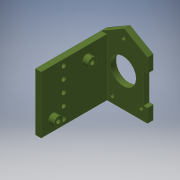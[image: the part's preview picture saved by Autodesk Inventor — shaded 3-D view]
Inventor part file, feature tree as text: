
AUTODESK INVENTOR PART (.ipt)
format: ipt  version: 2018 (Build 220112000, 112)  size: 209,408 bytes
history: native  units: in
note: dims shown in document units (in); Inventor stores cm internally (conversion verified against a paired STEP export)
features: extrude x8, sketch x6, plane x1, projected_geometry x1
ambient origin geometry x8: Origin, YZ Plane, XZ Plane, XY Plane, X Axis, Y Axis, Z Axis, Center Point
bodies: Solid1 (feature_tree)
feature tree (16):
  sketch  "Sketch1"  dims[d0=0.385in d1=0.385in]
  extrude  "Extrusion1"  Depth=0.385in
  extrude  "Extrusion2"  Depth=0.5in
  extrude  "Extrusion3"  Depth=0.5in
  extrude  "Extrusion4"  Depth=0.25in TaperAngle=0.0deg
  extrude  "Extrusion5"  Depth=0.5in
  extrude  "Extrusion7"  Depth=2.0in
  plane  "Work Plane1"
  extrude  "Extrusion12"  Depth=0.25in TaperAngle=0.0deg
  extrude  "Extrusion13"  Depth=0.3937in
  sketch  "Sketch2"  dims[d4=2.08in d5=0.5in]
  sketch  "Sketch3"  dims[d6=0.5in d7=0.5in]
  projected_geometry  "Projected Loop1"
  sketch  "Sketch5"  dims[d8=0.875in d9=0.25in d10=0.0in]
  sketch  "Sketch10"  dims[d11=0.5in d12=0.0in d13=0.1935in]
  sketch  "Sketch11"  dims[d14=0.5in d15=0.0in d16=2.0in d17=0.25in d18=0.0in d19=0.768in d20=0.699in d22=1.122in d23=2.5in d24=0.0in d25=0.25in d26=2.0in d27=0.25in d33=0.1935in d38=1.0in d39=0.0in d46=1.25in d47=1.25in d48=1.25in d49=1.25in d50=2.375in d51=1.0in d58=1.25in d77=0.1935in d78=0.25in d79=0.25in d80=1.9685in d82=0.5in d83=0.3937in d85=1.0in d87=1.0in d88=0.0in d89=30.0deg d90=30.0deg d91=1.4348in d92=0.02in d93=1.0in d94=0.0in]
